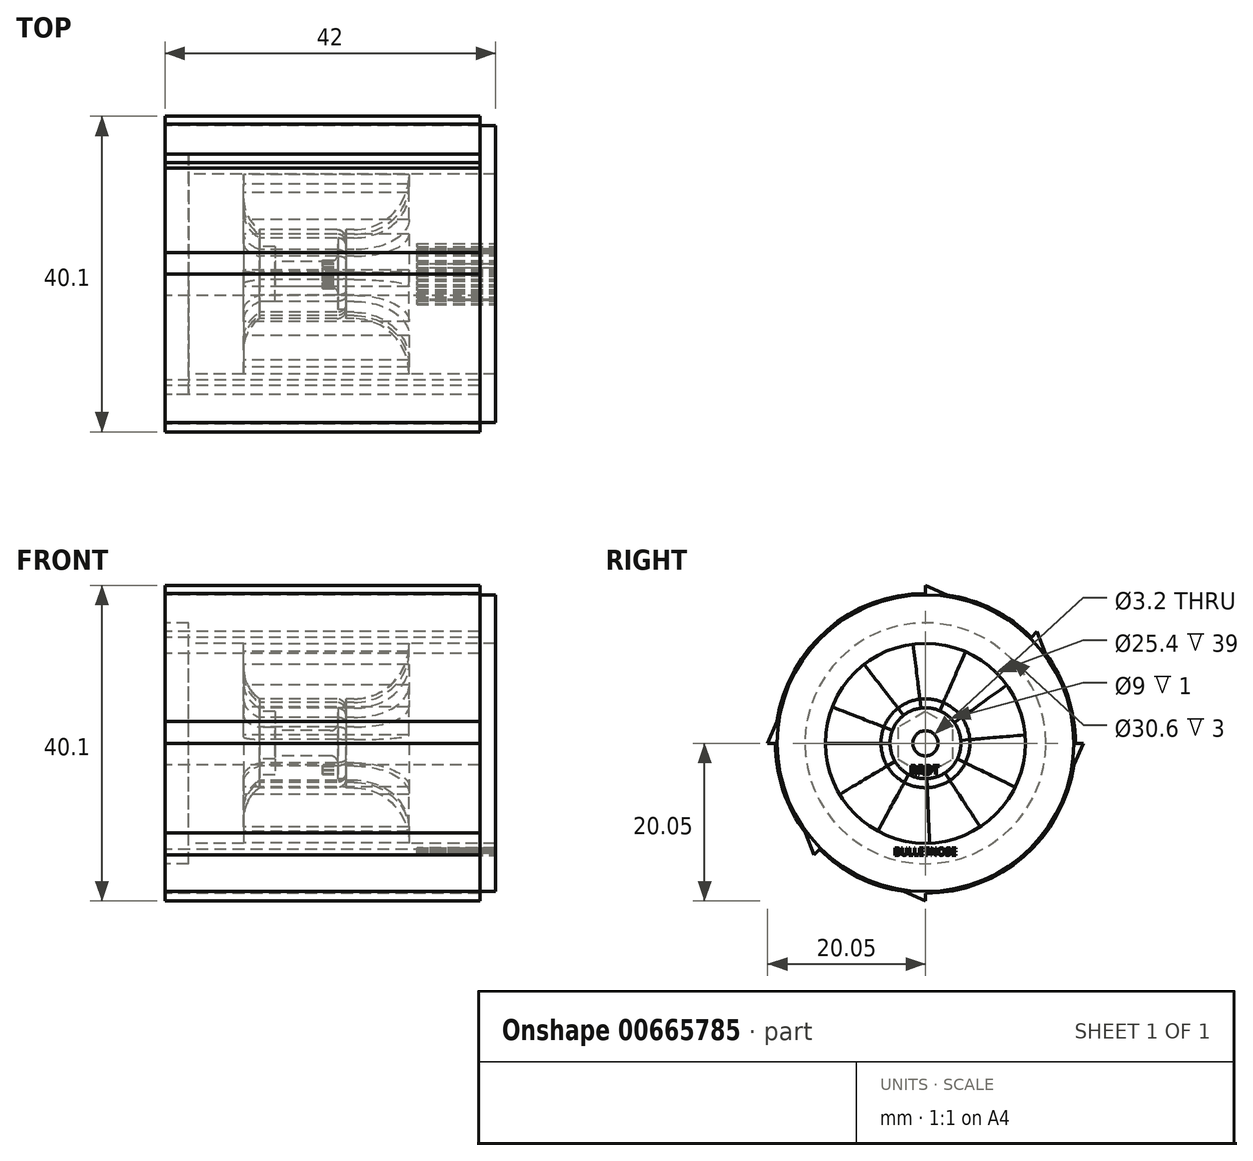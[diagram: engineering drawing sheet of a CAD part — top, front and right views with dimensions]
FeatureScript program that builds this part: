
annotation { "Feature Type Name" : "Feature", "Feature Type Description" : "" }
export const myFeature = defineFeature(function(context is Context, id is Id, definition is map)
    precondition{}
    {
        {
            var Q0;
            Q0=qCreatedBy(makeId("Right.planeOp"),FACE);
            var sketch = newSketch(context, id + "F0", { "sketchPlane" : qUnion([Q0])});
            skCircle(sketch, "E0", {"center": v(0, 0) * mm, "radius": 15.3 * mm});
            skCircle(sketch, "E1", {"center": v(0, 0) * mm, "radius": 12.7 * mm});
            skCircle(sketch, "E2", {"center": v(0, 0) * mm, "radius": 5.65 * mm});
            skLineSegment(sketch, "E3", {"start": v(-5.65, 0) * mm, "end": v(-12.7, 0) * mm});
            skLineSegment(sketch, "E4", {"start": v(-4.85, -2.9) * mm, "end": v(-10.9, -6.5) * mm});
            skLineSegment(sketch, "E5", {"start": v(-2.69, -4.97) * mm, "end": v(-6.04, -11.17) * mm});
            skLineSegment(sketch, "E6", {"start": v(0.23, -5.65) * mm, "end": v(0.53, -12.69) * mm});
            skLineSegment(sketch, "E7", {"start": v(5.63, 0.47) * mm, "end": v(12.66, 1.05) * mm});
            skLineSegment(sketch, "E8", {"start": v(3.1, -4.73) * mm, "end": v(6.95, -10.63) * mm});
            skLineSegment(sketch, "E9", {"start": v(4.6, 3.28) * mm, "end": v(10.33, 7.38) * mm});
            skLineSegment(sketch, "E10", {"start": v(5.08, -2.48) * mm, "end": v(11.41, -5.58) * mm});
            skLineSegment(sketch, "E11", {"start": v(2.27, 5.17) * mm, "end": v(5.1, 11.63) * mm});
            skLineSegment(sketch, "E12", {"start": v(-0.7, 5.6) * mm, "end": v(-1.58, 12.6) * mm});
            skLineSegment(sketch, "E13", {"start": v(-3.47, 4.46) * mm, "end": v(-7.8, 10.02) * mm});
            skLineSegment(sketch, "E14", {"start": v(-5.26, 2.05) * mm, "end": v(-11.83, 4.61) * mm});
            skCircle(sketch, "E15", {"center": v(0, 0) * mm, "radius": 1.6 * mm});
            skCircle(sketch, "E16", {"center": v(0, 0) * mm, "radius": 4.5 * mm});
            skCircle(sketch, "E17", {"center": v(0, 0) * mm, "radius": 19.05 * mm});
            skLineSegment(sketch, "E18", {"start": v(0, 19.05) * mm, "end": v(0, 20.05) * mm});
            skLineSegment(sketch, "E19", {"start": v(0, 20.05) * mm, "end": v(2.75, 18.85) * mm});
            skLineSegment(sketch, "E20", {"start": v(-19.05, 0) * mm, "end": v(-20.05, 0) * mm});
            skLineSegment(sketch, "E21", {"start": v(-20.05, 0) * mm, "end": v(-18.85, 2.75) * mm});
            skLineSegment(sketch, "E22", {"start": v(0, -19.05) * mm, "end": v(0, -20.05) * mm});
            skLineSegment(sketch, "E23", {"start": v(0, -20.05) * mm, "end": v(-2.75, -18.85) * mm});
            skLineSegment(sketch, "E24", {"start": v(19.05, 0) * mm, "end": v(20.05, 0) * mm});
            skLineSegment(sketch, "E25", {"start": v(20.05, 0) * mm, "end": v(18.85, -2.75) * mm});
            skLineSegment(sketch, "E26", {"start": v(13.47, 13.47) * mm, "end": v(14.17, 14.18) * mm});
            skLineSegment(sketch, "E27", {"start": v(14.17, 14.18) * mm, "end": v(15.27, 11.39) * mm});
            skLineSegment(sketch, "E28", {"start": v(-13.47, -13.47) * mm, "end": v(-14.17, -14.18) * mm});
            skLineSegment(sketch, "E29", {"start": v(-14.17, -14.18) * mm, "end": v(-15.27, -11.39) * mm});
            skSolve(sketch);
        }
        {
            var Q0;
            Q0=makeQuery(id+"F0.imprint","IMPRINT",FACE,{"disambiguationData":[TD([[makeQuery(id+"F0.imprint","IMPRINT",EDGE,{"derivedFrom":sQuery(id+"F0.wireOp",EDGE,"E0")}),1.0]])]});
            extrude(context, id + "F1", {"entities" : qUnion([Q0]), "depth" : 20 * mm, "offsetDistance" : 25 * mm, "hasSecondDirection" : true, "secondDirectionOppositeDirection" : true, "secondDirectionDepth" : 14 * mm});
        }
        {
            var Q0;
            Q0=makeQuery(id+"F0.imprint","IMPRINT",FACE,{"disambiguationData":[TD([[makeQuery(id+"F0.imprint","IMPRINT",EDGE,{"derivedFrom":sQuery(id+"F0.wireOp",EDGE,"E16")}),-1.0]])]});
            extrude(context, id + "F2", {"entities" : qUnion([Q0]), "depth" : 6 * mm, "offsetDistance" : 25 * mm});
        }
        {
            var Q0;
            Q0=makeQuery(id+"F0.imprint","IMPRINT",FACE,{"disambiguationData":[TD([[makeQuery(id+"F0.imprint","IMPRINT",EDGE,{"derivedFrom":sQuery(id+"F0.wireOp",EDGE,"E15")}),-1.0]])]});
            extrude(context, id + "F3", {"entities" : qUnion([Q0]), "operationType" : NewBodyOperationType.ADD, "depth" : 5 * mm, "offsetDistance" : 25 * mm, "hasSecondDirection" : true, "secondDirectionOppositeDirection" : true, "secondDirectionDepth" : 5 * mm});
        }
        {
            var Q0;
            {var subQ0=sQuery(id+"F0.wireOp",EDGE,"E3");Q0=makeQuery(id+"F0.imprint","IMPRINT",FACE,{"disambiguationData":[TD([[makeQuery(id+"F0.imprint","IMPRINT",EDGE,{"derivedFrom":subQ0}),1.0]])]});}
            var Q1;
            {var subQ0=sQuery(id+"F0.wireOp",EDGE,"E5");Q1=makeQuery(id+"F0.imprint","IMPRINT",FACE,{"disambiguationData":[TD([[makeQuery(id+"F0.imprint","IMPRINT",EDGE,{"derivedFrom":subQ0}),1.0]])]});}
            var Q2;
            {var subQ0=sQuery(id+"F0.wireOp",EDGE,"E8");Q2=makeQuery(id+"F0.imprint","IMPRINT",FACE,{"disambiguationData":[TD([[makeQuery(id+"F0.imprint","IMPRINT",EDGE,{"derivedFrom":subQ0}),1.0]])]});}
            var Q3;
            {var subQ0=sQuery(id+"F0.wireOp",EDGE,"E7");Q3=makeQuery(id+"F0.imprint","IMPRINT",FACE,{"disambiguationData":[TD([[makeQuery(id+"F0.imprint","IMPRINT",EDGE,{"derivedFrom":subQ0}),1.0]])]});}
            var Q4;
            {var subQ0=sQuery(id+"F0.wireOp",EDGE,"E11");Q4=makeQuery(id+"F0.imprint","IMPRINT",FACE,{"disambiguationData":[TD([[makeQuery(id+"F0.imprint","IMPRINT",EDGE,{"derivedFrom":subQ0}),1.0]])]});}
            var Q5;
            {var subQ0=sQuery(id+"F0.wireOp",EDGE,"E13");Q5=makeQuery(id+"F0.imprint","IMPRINT",FACE,{"disambiguationData":[TD([[makeQuery(id+"F0.imprint","IMPRINT",EDGE,{"derivedFrom":subQ0}),1.0]])]});}
            extrude(context, id + "F4", {"entities" : qUnion([Q0, Q1, Q2, Q3, Q4, Q5]), "operationType" : NewBodyOperationType.ADD, "depth" : 14 * mm, "offsetDistance" : 25 * mm, "hasSecondDirection" : true, "secondDirectionOppositeDirection" : true, "secondDirectionDepth" : 7 * mm});
        }
        {
            var Q0;
            Q0=makeQuery(id+"F0.imprint","IMPRINT",FACE,{"disambiguationData":[TD([[makeQuery(id+"F0.imprint","IMPRINT",EDGE,{"derivedFrom":sQuery(id+"F0.wireOp",EDGE,"E16")}),-1.0]])]});
            extrude(context, id + "F5", {"entities" : qUnion([Q0]), "operationType" : NewBodyOperationType.ADD, "oppositeDirection" : true, "depth" : 5 * mm, "offsetDistance" : 25 * mm});
        }
        {
            var Q0;
            Q0=makeQuery(id+"F3.opExtrude","CAP_FACE",FACE,{"disambiguationData":[OSD([sQuery(id+"F0.wireOp",EDGE,"E15"),sQuery(id+"F0.wireOp",EDGE,"E16")])],"isStart":false});
            var sketch = newSketch(context, id + "F6", { "sketchPlane" : qUnion([Q0])});
            skText(sketch, "E30", { "text": "RRDT", "fontName": "DroidSansMono.ttf"});
            const initialGuessF6  = {"E30": [-0.002, -0.00395, 1, 0, 0.00115]};
            skSetInitialGuess(sketch, initialGuessF6);
            skSolve(sketch);
        }
        {
            var Q0;
            Q0 = qSketchRegion(id + "F6", true);
            extrude(context, id + "F7", {"entities" : qUnion([Q0]), "operationType" : NewBodyOperationType.REMOVE, "oppositeDirection" : true, "depth" : 2 * mm, "offsetDistance" : 25 * mm});
        }
        {
            var Q0;
            {var subQ0=sQuery(id+"F0.wireOp",EDGE,"E2");Q0=makeQuery(id+"F4.opExtrude","CAP_EDGE",EDGE,{"disambiguationData":[OSD([subQ0]),TDD([makeQuery(id+"F0.imprint","IMPRINT",EDGE,{"disambiguationData":[TD([[makeQuery(id+"F0.imprint","INTERSECT",VERTEX,{"derivedFrom":[subQ0,sQuery(id+"F0.wireOp",EDGE,"E3")]}),-1.0]])],"derivedFrom":subQ0})])],"isStart":false});}
            fillet(context, id + "F8", {"entities" : qUnion([Q0]), "radius" : 7 * mm, "tangentPropagation" : true, "allowEdgeOverflow" : false});
        }
        {
            var Q0;
            {var subQ0=sQuery(id+"F0.wireOp",EDGE,"E2");Q0=makeQuery(id+"F4.opExtrude","CAP_EDGE",EDGE,{"disambiguationData":[OSD([subQ0]),TDD([makeQuery(id+"F0.imprint","IMPRINT",EDGE,{"disambiguationData":[TD([[makeQuery(id+"F0.imprint","INTERSECT",VERTEX,{"derivedFrom":[subQ0,sQuery(id+"F0.wireOp",EDGE,"E5")]}),-1.0]])],"derivedFrom":subQ0})])],"isStart":false});}
            var Q1;
            {var subQ0=sQuery(id+"F0.wireOp",EDGE,"E2");Q1=makeQuery(id+"F4.opExtrude","CAP_EDGE",EDGE,{"disambiguationData":[OSD([subQ0]),TDD([makeQuery(id+"F0.imprint","IMPRINT",EDGE,{"disambiguationData":[TD([[makeQuery(id+"F0.imprint","INTERSECT",VERTEX,{"derivedFrom":[subQ0,sQuery(id+"F0.wireOp",EDGE,"E8")]}),-1.0]])],"derivedFrom":subQ0})])],"isStart":false});}
            var Q2;
            {var subQ0=sQuery(id+"F0.wireOp",EDGE,"E2");Q2=makeQuery(id+"F4.opExtrude","CAP_EDGE",EDGE,{"disambiguationData":[OSD([subQ0]),TDD([makeQuery(id+"F0.imprint","IMPRINT",EDGE,{"disambiguationData":[TD([[makeQuery(id+"F0.imprint","INTERSECT",VERTEX,{"derivedFrom":[subQ0,sQuery(id+"F0.wireOp",EDGE,"E7")]}),-1.0]])],"derivedFrom":subQ0})])],"isStart":false});}
            var Q3;
            {var subQ0=sQuery(id+"F0.wireOp",EDGE,"E2");Q3=makeQuery(id+"F4.opExtrude","CAP_EDGE",EDGE,{"disambiguationData":[OSD([subQ0]),TDD([makeQuery(id+"F0.imprint","IMPRINT",EDGE,{"disambiguationData":[TD([[makeQuery(id+"F0.imprint","INTERSECT",VERTEX,{"derivedFrom":[subQ0,sQuery(id+"F0.wireOp",EDGE,"E11")]}),-1.0]])],"derivedFrom":subQ0})])],"isStart":false});}
            var Q4;
            {var subQ0=sQuery(id+"F0.wireOp",EDGE,"E2");Q4=makeQuery(id+"F4.opExtrude","CAP_EDGE",EDGE,{"disambiguationData":[OSD([subQ0]),TDD([makeQuery(id+"F0.imprint","IMPRINT",EDGE,{"disambiguationData":[TD([[makeQuery(id+"F0.imprint","INTERSECT",VERTEX,{"derivedFrom":[subQ0,sQuery(id+"F0.wireOp",EDGE,"E13")]}),-1.0]])],"derivedFrom":subQ0})])],"isStart":false});}
            fillet(context, id + "F9", {"entities" : qUnion([Q0, Q1, Q2, Q3, Q4]), "radius" : 7 * mm, "tangentPropagation" : true, "allowEdgeOverflow" : false});
        }
        {
            var Q0;
            {var subQ0=sQuery(id+"F0.wireOp",EDGE,"E2");var subQ1=sQuery(id+"F0.wireOp",EDGE,"E4");var subQ2=makeQuery(id+"F2.opExtrude","SWEPT_FACE",FACE,{"disambiguationData":[OSD([subQ0])]});var subQ3=makeQuery(id+"F2.opExtrude","CAP_FACE",FACE,{"disambiguationData":[OSD([subQ0,sQuery(id+"F0.wireOp",EDGE,"E16")])],"isStart":false});Q0=makeQuery(id+"F4.boolean.opBoolean","SPLIT",EDGE,{"disambiguationData":[topologyDisambiguationEdgeConnected([subQ2,subQ3]),TD([makeQuery(id+"F4.opExtrude","SWEPT_FACE",FACE,{"disambiguationData":[OSD([subQ1])]})])],"derivedFrom":makeQuery(id+"F2.opExtrude","CAP_EDGE",EDGE,{"disambiguationData":[OSD([subQ0])],"isStart":false})});}
            var Q1;
            {var subQ0=sQuery(id+"F0.wireOp",EDGE,"E3");var subQ1=sQuery(id+"F0.wireOp",EDGE,"E2");var subQ2=makeQuery(id+"F2.opExtrude","SWEPT_FACE",FACE,{"disambiguationData":[OSD([subQ1])]});var subQ4=makeQuery(id+"F2.opExtrude","CAP_FACE",FACE,{"disambiguationData":[OSD([subQ1,sQuery(id+"F0.wireOp",EDGE,"E16")])],"isStart":false});Q1=makeQuery(id+"F4.boolean.opBoolean","SPLIT",EDGE,{"disambiguationData":[topologyDisambiguationEdgeConnected([subQ2,subQ4]),TD([makeQuery(id+"F4.opExtrude","SWEPT_FACE",FACE,{"disambiguationData":[OSD([subQ0])]})])],"derivedFrom":makeQuery(id+"F2.opExtrude","CAP_EDGE",EDGE,{"disambiguationData":[OSD([subQ1])],"isStart":false})});}
            var Q2;
            {var subQ1=sQuery(id+"F0.wireOp",EDGE,"E2");var subQ2=sQuery(id+"F0.wireOp",EDGE,"E12");var subQ3=makeQuery(id+"F2.opExtrude","CAP_FACE",FACE,{"disambiguationData":[OSD([subQ1,sQuery(id+"F0.wireOp",EDGE,"E16")])],"isStart":false});var subQ4=makeQuery(id+"F2.opExtrude","SWEPT_FACE",FACE,{"disambiguationData":[OSD([subQ1])]});Q2=makeQuery(id+"F4.boolean.opBoolean","SPLIT",EDGE,{"disambiguationData":[topologyDisambiguationEdgeConnected([subQ4,subQ3]),TD([makeQuery(id+"F4.opExtrude","SWEPT_FACE",FACE,{"disambiguationData":[OSD([subQ2])]})])],"derivedFrom":makeQuery(id+"F2.opExtrude","CAP_EDGE",EDGE,{"disambiguationData":[OSD([subQ1])],"isStart":false})});}
            var Q3;
            {var subQ0=sQuery(id+"F0.wireOp",EDGE,"E2");var subQ1=sQuery(id+"F0.wireOp",EDGE,"E9");var subQ3=makeQuery(id+"F2.opExtrude","CAP_FACE",FACE,{"disambiguationData":[OSD([subQ0,sQuery(id+"F0.wireOp",EDGE,"E16")])],"isStart":false});var subQ4=makeQuery(id+"F2.opExtrude","SWEPT_FACE",FACE,{"disambiguationData":[OSD([subQ0])]});Q3=makeQuery(id+"F4.boolean.opBoolean","SPLIT",EDGE,{"disambiguationData":[topologyDisambiguationEdgeConnected([subQ4,subQ3]),TD([makeQuery(id+"F4.opExtrude","SWEPT_FACE",FACE,{"disambiguationData":[OSD([subQ1])]})])],"derivedFrom":makeQuery(id+"F2.opExtrude","CAP_EDGE",EDGE,{"disambiguationData":[OSD([subQ0])],"isStart":false})});}
            var Q4;
            {var subQ0=sQuery(id+"F0.wireOp",EDGE,"E2");var subQ2=makeQuery(id+"F2.opExtrude","CAP_FACE",FACE,{"disambiguationData":[OSD([subQ0,sQuery(id+"F0.wireOp",EDGE,"E16")])],"isStart":false});var subQ3=sQuery(id+"F0.wireOp",EDGE,"E7");var subQ4=makeQuery(id+"F2.opExtrude","SWEPT_FACE",FACE,{"disambiguationData":[OSD([subQ0])]});Q4=makeQuery(id+"F4.boolean.opBoolean","SPLIT",EDGE,{"disambiguationData":[topologyDisambiguationEdgeConnected([subQ4,subQ2]),TD([makeQuery(id+"F4.opExtrude","SWEPT_FACE",FACE,{"disambiguationData":[OSD([subQ3])]})])],"derivedFrom":makeQuery(id+"F2.opExtrude","CAP_EDGE",EDGE,{"disambiguationData":[OSD([subQ0])],"isStart":false})});}
            var Q5;
            {var subQ1=sQuery(id+"F0.wireOp",EDGE,"E2");var subQ2=makeQuery(id+"F2.opExtrude","CAP_FACE",FACE,{"disambiguationData":[OSD([subQ1,sQuery(id+"F0.wireOp",EDGE,"E16")])],"isStart":false});var subQ3=sQuery(id+"F0.wireOp",EDGE,"E6");var subQ4=makeQuery(id+"F2.opExtrude","SWEPT_FACE",FACE,{"disambiguationData":[OSD([subQ1])]});Q5=makeQuery(id+"F4.boolean.opBoolean","SPLIT",EDGE,{"disambiguationData":[topologyDisambiguationEdgeConnected([subQ4,subQ2]),TD([makeQuery(id+"F4.opExtrude","SWEPT_FACE",FACE,{"disambiguationData":[OSD([subQ3])]})])],"derivedFrom":makeQuery(id+"F2.opExtrude","CAP_EDGE",EDGE,{"disambiguationData":[OSD([subQ1])],"isStart":false})});}
            fillet(context, id + "F10", {"entities" : qUnion([Q0, Q1, Q2, Q3, Q4, Q5]), "radius" : 1.15 * mm, "tangentPropagation" : true, "allowEdgeOverflow" : false});
        }
        {
            var Q0;
            Q0=makeQuery(id+"F3.opExtrude","CAP_EDGE",EDGE,{"disambiguationData":[OSD([sQuery(id+"F0.wireOp",EDGE,"E15")])],"isStart":false});
            fillet(context, id + "F11", {"entities" : qUnion([Q0]), "radius" : 1 * mm, "tangentPropagation" : true, "allowEdgeOverflow" : false});
        }
        {
            var Q0;
            {var subQ0=sQuery(id+"F0.wireOp",EDGE,"E2");Q0=makeQuery(id+"F4.opExtrude","CAP_EDGE",EDGE,{"disambiguationData":[OSD([subQ0]),TDD([makeQuery(id+"F0.imprint","IMPRINT",EDGE,{"disambiguationData":[TD([[makeQuery(id+"F0.imprint","INTERSECT",VERTEX,{"derivedFrom":[subQ0,sQuery(id+"F0.wireOp",EDGE,"E7")]}),-1.0]])],"derivedFrom":subQ0})])],"isStart":true});}
            var Q1;
            {var subQ0=sQuery(id+"F0.wireOp",EDGE,"E2");Q1=makeQuery(id+"F4.opExtrude","CAP_EDGE",EDGE,{"disambiguationData":[OSD([subQ0]),TDD([makeQuery(id+"F0.imprint","IMPRINT",EDGE,{"disambiguationData":[TD([[makeQuery(id+"F0.imprint","INTERSECT",VERTEX,{"derivedFrom":[subQ0,sQuery(id+"F0.wireOp",EDGE,"E8")]}),-1.0]])],"derivedFrom":subQ0})])],"isStart":true});}
            var Q2;
            {var subQ0=sQuery(id+"F0.wireOp",EDGE,"E2");Q2=makeQuery(id+"F4.opExtrude","CAP_EDGE",EDGE,{"disambiguationData":[OSD([subQ0]),TDD([makeQuery(id+"F0.imprint","IMPRINT",EDGE,{"disambiguationData":[TD([[makeQuery(id+"F0.imprint","INTERSECT",VERTEX,{"derivedFrom":[subQ0,sQuery(id+"F0.wireOp",EDGE,"E5")]}),-1.0]])],"derivedFrom":subQ0})])],"isStart":true});}
            var Q3;
            {var subQ0=sQuery(id+"F0.wireOp",EDGE,"E2");Q3=makeQuery(id+"F4.opExtrude","CAP_EDGE",EDGE,{"disambiguationData":[OSD([subQ0]),TDD([makeQuery(id+"F0.imprint","IMPRINT",EDGE,{"disambiguationData":[TD([[makeQuery(id+"F0.imprint","INTERSECT",VERTEX,{"derivedFrom":[subQ0,sQuery(id+"F0.wireOp",EDGE,"E3")]}),-1.0]])],"derivedFrom":subQ0})])],"isStart":true});}
            var Q4;
            {var subQ0=sQuery(id+"F0.wireOp",EDGE,"E2");Q4=makeQuery(id+"F4.opExtrude","CAP_EDGE",EDGE,{"disambiguationData":[OSD([subQ0]),TDD([makeQuery(id+"F0.imprint","IMPRINT",EDGE,{"disambiguationData":[TD([[makeQuery(id+"F0.imprint","INTERSECT",VERTEX,{"derivedFrom":[subQ0,sQuery(id+"F0.wireOp",EDGE,"E13")]}),-1.0]])],"derivedFrom":subQ0})])],"isStart":true});}
            var Q5;
            {var subQ0=sQuery(id+"F0.wireOp",EDGE,"E2");Q5=makeQuery(id+"F4.opExtrude","CAP_EDGE",EDGE,{"disambiguationData":[OSD([subQ0]),TDD([makeQuery(id+"F0.imprint","IMPRINT",EDGE,{"disambiguationData":[TD([[makeQuery(id+"F0.imprint","INTERSECT",VERTEX,{"derivedFrom":[subQ0,sQuery(id+"F0.wireOp",EDGE,"E11")]}),-1.0]])],"derivedFrom":subQ0})])],"isStart":true});}
            fillet(context, id + "F12", {"entities" : qUnion([Q0, Q1, Q2, Q3, Q4, Q5]), "radius" : 5 * mm, "tangentPropagation" : true, "allowEdgeOverflow" : false});
        }
        {
            var Q0;
            Q0=makeQuery(id+"F3.opExtrude","CAP_FACE",FACE,{"disambiguationData":[OSD([sQuery(id+"F0.wireOp",EDGE,"E15"),sQuery(id+"F0.wireOp",EDGE,"E16")])],"isStart":true});
            var sketch = newSketch(context, id + "F13", { "sketchPlane" : qUnion([Q0])});
            skCircle(sketch, "E31.cCircle", {"center": v(0, 0) * mm, "radius": 3.5 * mm, "construction": true});
            skLineSegment(sketch, "E31.0", {"start": v(3.5, -2.02) * mm, "end": v(0, -4.04) * mm});
            skLineSegment(sketch, "E31.1", {"start": v(0, -4.04) * mm, "end": v(-3.5, -2.02) * mm});
            skLineSegment(sketch, "E31.2", {"start": v(-3.5, -2.02) * mm, "end": v(-3.5, 2.02) * mm});
            skLineSegment(sketch, "E31.3", {"start": v(-3.5, 2.02) * mm, "end": v(0, 4.04) * mm});
            skLineSegment(sketch, "E31.4", {"start": v(0, 4.04) * mm, "end": v(3.5, 2.02) * mm});
            skLineSegment(sketch, "E31.5", {"start": v(3.5, 2.02) * mm, "end": v(3.5, -2.02) * mm});
            skPoint(sketch, "E31.0.midPoint", {"position": v(1.75, -3.03) * mm});
            skSolve(sketch);
        }
        {
            var Q0;
            Q0=makeQuery(id+"F13.imprint","IMPRINT",FACE,{"disambiguationData":[TD([[makeQuery(id+"F13.imprint","IMPRINT",EDGE,{"derivedFrom":sQuery(id+"F13.wireOp",EDGE,"E31.0")}),-1.0]])]});
            extrude(context, id + "F14", {"entities" : qUnion([Q0]), "operationType" : NewBodyOperationType.REMOVE, "oppositeDirection" : true, "depth" : 2 * mm, "offsetDistance" : 25 * mm});
        }
        {
            var Q0;
            Q0=makeQuery(id+"F0.imprint","IMPRINT",FACE,{"disambiguationData":[TD([[makeQuery(id+"F0.imprint","IMPRINT",EDGE,{"derivedFrom":sQuery(id+"F0.wireOp",EDGE,"E0")}),-1.0]])]});
            extrude(context, id + "F15", {"entities" : qUnion([Q0]), "operationType" : NewBodyOperationType.ADD, "depth" : 23 * mm, "offsetDistance" : 25 * mm, "hasSecondDirection" : true, "secondDirectionOppositeDirection" : true, "secondDirectionDepth" : 17 * mm});
        }
        {
            var Q0;
            Q0=makeQuery(id+"F1.opExtrude","CAP_FACE",FACE,{"disambiguationData":[OSD([sQuery(id+"F0.wireOp",EDGE,"E0"),sQuery(id+"F0.wireOp",EDGE,"E1")])],"isStart":false});
            var sketch = newSketch(context, id + "F16", { "sketchPlane" : qUnion([Q0])});
            skText(sketch, "E32", { "text": "BULLETNOSE", "fontName": "OpenSans-Regular.ttf"});
            const initialGuessF16  = {"E32": [-0.004, -0.01423, 1, 0, 0.00093]};
            skSetInitialGuess(sketch, initialGuessF16);
            skSolve(sketch);
        }
        {
            var Q0;
            Q0 = qSketchRegion(id + "F16", true);
            extrude(context, id + "F17", {"entities" : qUnion([Q0]), "operationType" : NewBodyOperationType.REMOVE, "oppositeDirection" : true, "depth" : 5 * mm, "offsetDistance" : 25 * mm});
        }
        {
            var Q0;
            {var subQ0=sQuery(id+"F0.wireOp",EDGE,"E24");Q0=makeQuery(id+"F0.imprint","IMPRINT",FACE,{"disambiguationData":[TD([[makeQuery(id+"F0.imprint","IMPRINT",EDGE,{"derivedFrom":subQ0}),-1.0]])]});}
            var Q1;
            {var subQ0=sQuery(id+"F0.wireOp",EDGE,"E26");Q1=makeQuery(id+"F0.imprint","IMPRINT",FACE,{"disambiguationData":[TD([[makeQuery(id+"F0.imprint","IMPRINT",EDGE,{"derivedFrom":subQ0}),-1.0]])]});}
            var Q2;
            {var subQ0=sQuery(id+"F0.wireOp",EDGE,"E18");Q2=makeQuery(id+"F0.imprint","IMPRINT",FACE,{"disambiguationData":[TD([[makeQuery(id+"F0.imprint","IMPRINT",EDGE,{"derivedFrom":subQ0}),-1.0]])]});}
            var Q3;
            {var subQ0=sQuery(id+"F0.wireOp",EDGE,"E22");Q3=makeQuery(id+"F0.imprint","IMPRINT",FACE,{"disambiguationData":[TD([[makeQuery(id+"F0.imprint","IMPRINT",EDGE,{"derivedFrom":subQ0}),-1.0]])]});}
            var Q4;
            {var subQ0=sQuery(id+"F0.wireOp",EDGE,"E28");Q4=makeQuery(id+"F0.imprint","IMPRINT",FACE,{"disambiguationData":[TD([[makeQuery(id+"F0.imprint","IMPRINT",EDGE,{"derivedFrom":subQ0}),-1.0]])]});}
            var Q5;
            {var subQ0=sQuery(id+"F0.wireOp",EDGE,"E20");Q5=makeQuery(id+"F0.imprint","IMPRINT",FACE,{"disambiguationData":[TD([[makeQuery(id+"F0.imprint","IMPRINT",EDGE,{"derivedFrom":subQ0}),-1.0]])]});}
            extrude(context, id + "F18", {"entities" : qUnion([Q0, Q1, Q2, Q3, Q4, Q5]), "operationType" : NewBodyOperationType.ADD, "depth" : 23 * mm, "offsetDistance" : 25 * mm, "hasSecondDirection" : true, "secondDirectionOppositeDirection" : true, "secondDirectionDepth" : 17 * mm});
        }
        {
            var Q0;
            {var subQ0=sQuery(id+"F0.wireOp",EDGE,"E1");var subQ1=sQuery(id+"F0.wireOp",EDGE,"E0");Q0=makeQuery(id+"F17.boolean.opBoolean","SPLIT",FACE,{"disambiguationData":[TD([makeQuery(id+"F1.opExtrude","SWEPT_FACE",FACE,{"disambiguationData":[OSD([subQ0])]})])],"derivedFrom":makeQuery(id+"F1.opExtrude","CAP_FACE",FACE,{"disambiguationData":[OSD([subQ1,subQ0])],"isStart":false})});}
            extrude(context, id + "F19", {"entities" : qUnion([Q0]), "operationType" : NewBodyOperationType.ADD, "depth" : 5 * mm, "offsetDistance" : 25 * mm});
        }
        {
            var Q0;
            Q0=qCreatedBy(makeId("Front.planeOp"),FACE);
            var sketch = newSketch(context, id + "F20", { "sketchPlane" : qUnion([Q0])});
            skLineSegment(sketch, "E33.bottom", {"start": v(23, 18.85) * mm, "end": v(25, 18.85) * mm});
            skLineSegment(sketch, "E33.top", {"start": v(23, 15.25) * mm, "end": v(25, 15.25) * mm});
            skLineSegment(sketch, "E33.left", {"start": v(23, 18.85) * mm, "end": v(23, 15.25) * mm});
            skLineSegment(sketch, "E33.right", {"start": v(25, 18.85) * mm, "end": v(25, 15.25) * mm});
            skSolve(sketch);
        }
        {
            var Q0;
            Q0=makeQuery(id+"F20.imprint","IMPRINT",FACE,{"disambiguationData":[TD([[makeQuery(id+"F20.imprint","IMPRINT",EDGE,{"derivedFrom":sQuery(id+"F20.wireOp",EDGE,"E33.bottom")}),-1.0]])]});
            var Q1;
            Q1=makeQuery(id+"F19.opExtrude","CAP_EDGE",EDGE,{"disambiguationData":[OSD([sQuery(id+"F0.wireOp",EDGE,"E0")])],"isStart":false});
            revolve(context, id + "F21", {"operationType" : NewBodyOperationType.ADD, "entities" : qUnion([Q0]), "axis" : qUnion([Q1]), "revolveType" : RevolveType.FULL});
        }
        {
            var Q0;
            Q0=makeQuery(id+"F17.boolean.opBoolean","SPLIT",FACE,{"disambiguationData":[TD([makeQuery(id+"F17.opExtrude","SWEPT_FACE",FACE,{"disambiguationData":[OSD([sQuery(id+"F16.wireOp",EDGE,"E32.sketch_text.stroke-94")])]})])],"derivedFrom":makeQuery(id+"F1.opExtrude","CAP_FACE",FACE,{"disambiguationData":[OSD([sQuery(id+"F0.wireOp",EDGE,"E0"),sQuery(id+"F0.wireOp",EDGE,"E1")])],"isStart":false})});
            var Q1;
            Q1=makeQuery(id+"F17.boolean.opBoolean","SPLIT",FACE,{"disambiguationData":[TD([makeQuery(id+"F17.opExtrude","SWEPT_FACE",FACE,{"disambiguationData":[OSD([sQuery(id+"F16.wireOp",EDGE,"E32.sketch_text.stroke-18")])]})])],"derivedFrom":makeQuery(id+"F1.opExtrude","CAP_FACE",FACE,{"disambiguationData":[OSD([sQuery(id+"F0.wireOp",EDGE,"E0"),sQuery(id+"F0.wireOp",EDGE,"E1")])],"isStart":false})});
            var Q2;
            Q2=makeQuery(id+"F17.boolean.opBoolean","SPLIT",FACE,{"disambiguationData":[TD([makeQuery(id+"F17.opExtrude","SWEPT_FACE",FACE,{"disambiguationData":[OSD([sQuery(id+"F16.wireOp",EDGE,"E32.sketch_text.stroke-11")])]})])],"derivedFrom":makeQuery(id+"F1.opExtrude","CAP_FACE",FACE,{"disambiguationData":[OSD([sQuery(id+"F0.wireOp",EDGE,"E0"),sQuery(id+"F0.wireOp",EDGE,"E1")])],"isStart":false})});
            extrude(context, id + "F22", {"entities" : qUnion([Q0, Q1, Q2]), "operationType" : NewBodyOperationType.ADD, "depth" : 5 * mm, "offsetDistance" : 25 * mm});
        }
    });
